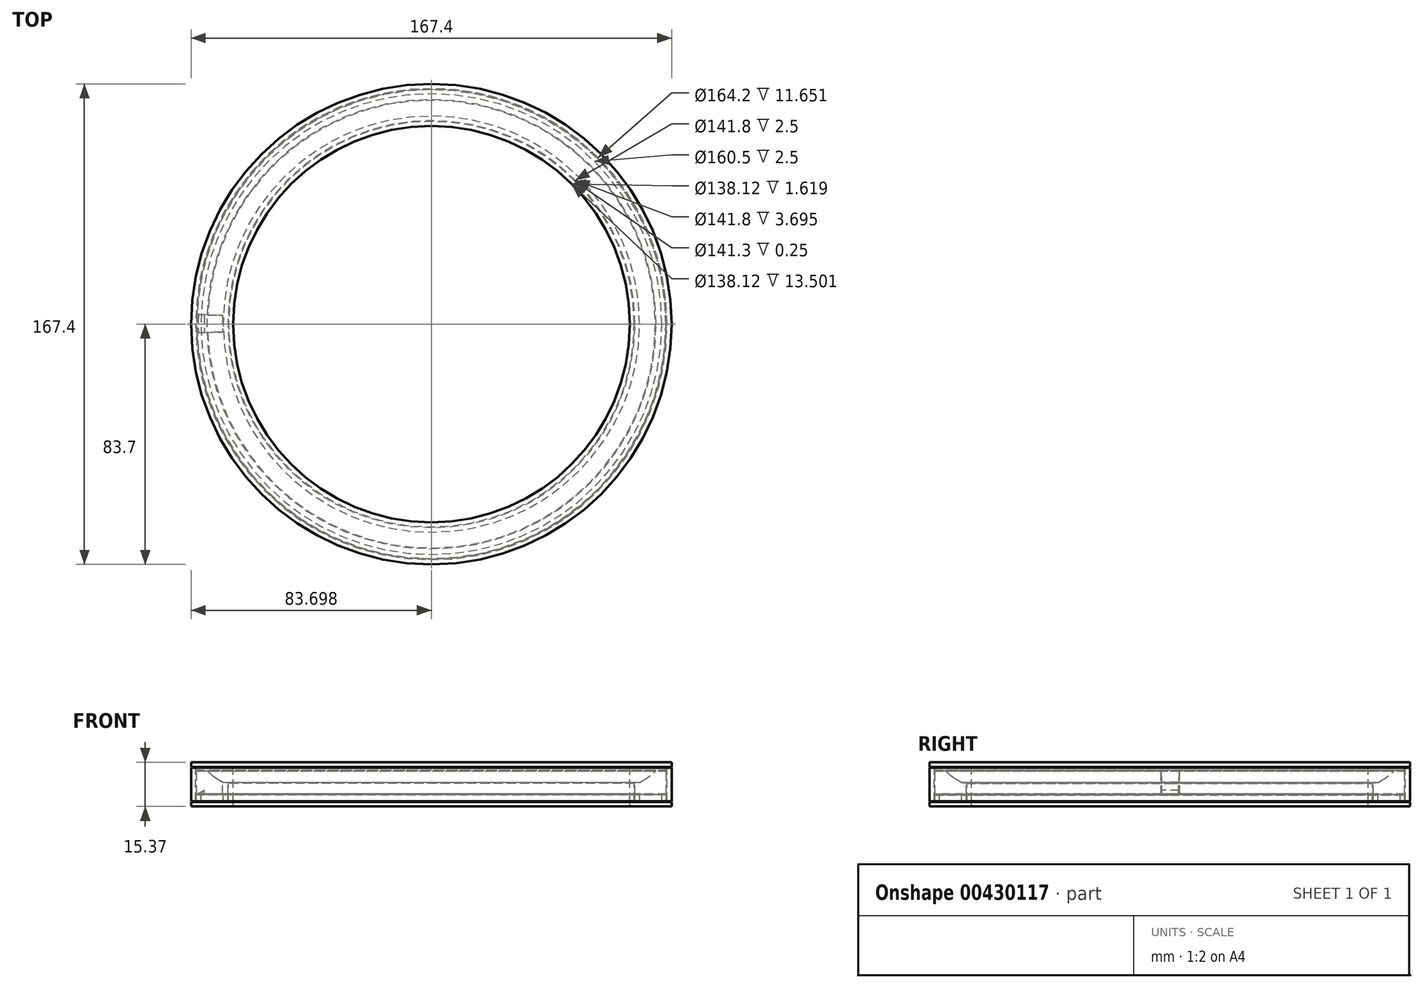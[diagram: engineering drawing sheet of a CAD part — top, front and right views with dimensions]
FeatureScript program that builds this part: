
annotation { "Feature Type Name" : "Feature", "Feature Type Description" : "" }
export const myFeature = defineFeature(function(context is Context, id is Id, definition is map)
    precondition{}
    {
        {
            var Q0;
            Q0=qCreatedBy(makeId("Front.planeOp"),FACE);
            var sketch = newSketch(context, id + "F0", { "sketchPlane" : qUnion([Q0])});
            skLineSegment(sketch, "E0", {"start": v(49.07, 29.5) * mm, "end": v(49.07, -21.25) * mm, "construction": true});
            skLineSegment(sketch, "E1", {"start": v(-23.43, 29.5) * mm, "end": v(-23.43, -21.25) * mm, "construction": true});
            skLineSegment(sketch, "E2", {"start": v(-30.18, 1.62) * mm, "end": v(-23.68, 1.62) * mm, "construction": true});
            skLineSegment(sketch, "E3", {"start": v(-23.68, 1.62) * mm, "end": v(-23.68, 4.12) * mm, "construction": true});
            skLineSegment(sketch, "E4", {"start": v(-23.68, 4.12) * mm, "end": v(-30.18, 4.12) * mm, "construction": true});
            skLineSegment(sketch, "E5", {"start": v(-30.18, 4.12) * mm, "end": v(-30.18, 1.62) * mm, "construction": true});
            skLineSegment(sketch, "E6", {"start": v(-29.18, 4.12) * mm, "end": v(-29.18, 4.92) * mm, "construction": true});
            skLineSegment(sketch, "E7", {"start": v(-29.18, 4.92) * mm, "end": v(-24.68, 4.92) * mm, "construction": true});
            skLineSegment(sketch, "E8", {"start": v(-24.68, 4.92) * mm, "end": v(-24.68, 4.12) * mm, "construction": true});
            skLineSegment(sketch, "E9", {"start": v(-35.93, 29.5) * mm, "end": v(-35.93, -21.25) * mm, "construction": true});
            skLineSegment(sketch, "E10", {"start": v(-31.18, 1.62) * mm, "end": v(-23.43, 1.62) * mm});
            skLineSegment(sketch, "E11", {"start": v(-31.18, 1.62) * mm, "end": v(-31.18, 4.12) * mm});
            skLineSegment(sketch, "E12", {"start": v(-34.74, 0.02) * mm, "end": v(-21.83, 0.02) * mm});
            skLineSegment(sketch, "E13", {"start": v(-23.43, 1.62) * mm, "end": v(-23.43, 3.24) * mm});
            skLineSegment(sketch, "E14", {"start": v(-23.43, 4.12) * mm, "end": v(-21.83, 4.12) * mm});
            skLineSegment(sketch, "E15", {"start": v(-21.83, 4.12) * mm, "end": v(-21.83, 0.02) * mm});
            skLineSegment(sketch, "E16", {"start": v(-24.68, 4.92) * mm, "end": v(-24.68, 12.8) * mm, "construction": true});
            skLineSegment(sketch, "E17", {"start": v(-29.18, 4.92) * mm, "end": v(-29.18, 12.8) * mm, "construction": true});
            skLineSegment(sketch, "E18", {"start": v(-82.01, -1.66) * mm, "end": v(-82.01, 10.37) * mm, "construction": true});
            skLineSegment(sketch, "E19", {"start": v(-23.43, 4.12) * mm, "end": v(-23.43, 1.62) * mm});
            skLineSegment(sketch, "E20", {"start": v(-72.42, 0.02) * mm, "end": v(839.7, 0.02) * mm, "construction": true});
            skLineSegment(sketch, "E21", {"start": v(-21.58, 1.87) * mm, "end": v(-21.58, 20.5) * mm});
            skLineSegment(sketch, "E22", {"start": v(-20, 1.87) * mm, "end": v(-20, 15.37) * mm});
            skLineSegment(sketch, "E23", {"start": v(-20, 15.37) * mm, "end": v(-34.63, 15.37) * mm});
            skLineSegment(sketch, "E24", {"start": v(-34.63, 13.52) * mm, "end": v(-33.03, 13.52) * mm});
            skLineSegment(sketch, "E25", {"start": v(-33.03, 13.52) * mm, "end": v(-33.03, 1.87) * mm});
            skLineSegment(sketch, "E26", {"start": v(-33.03, 1.87) * mm, "end": v(-34.63, 1.87) * mm});
            skLineSegment(sketch, "E27", {"start": v(-34.63, 1.87) * mm, "end": v(-34.63, 13.52) * mm});
            skLineSegment(sketch, "E28", {"start": v(-34.63, 0.02) * mm, "end": v(-34.74, 0.02) * mm});
            skLineSegment(sketch, "E29", {"start": v(-34.63, 0.02) * mm, "end": v(-34.63, 1.62) * mm});
            skLineSegment(sketch, "E30", {"start": v(-34.63, 1.62) * mm, "end": v(-32.78, 1.62) * mm});
            skLineSegment(sketch, "E31", {"start": v(-34.63, 15.37) * mm, "end": v(-34.63, 13.77) * mm});
            skLineSegment(sketch, "E32", {"start": v(-34.63, 13.77) * mm, "end": v(-32.78, 13.77) * mm});
            skLineSegment(sketch, "E33", {"start": v(-36.84, 4.37) * mm, "end": v(-22.3, 4.37) * mm, "construction": true});
            skLineSegment(sketch, "E34", {"start": v(-32.78, 1.62) * mm, "end": v(-32.78, 2.82) * mm});
            skLineSegment(sketch, "E35", {"start": v(-32.78, 13.77) * mm, "end": v(-32.78, 12.57) * mm});
            skLineSegment(sketch, "E36", {"start": v(-32.78, 12.57) * mm, "end": v(-28.4, 12.57) * mm});
            skLineSegment(sketch, "E37", {"start": v(-23.43, 8.31) * mm, "end": v(-21.58, 8.31) * mm});
            skLineSegment(sketch, "E38", {"start": v(-21.83, 4.37) * mm, "end": v(-31.4, 4.37) * mm});
            skLineSegment(sketch, "E39", {"start": v(-31.4, 4.37) * mm, "end": v(-32.78, 4.37) * mm});
            skLineSegment(sketch, "E40.0", {"start": v(-32.78, 12.32) * mm, "end": v(-28.4, 12.32) * mm});
            skLineSegment(sketch, "E41", {"start": v(-32.78, 12.32) * mm, "end": v(-32.78, 4.37) * mm});
            skLineSegment(sketch, "E42", {"start": v(-23.43, 8.31) * mm, "end": v(-24.68, 9.04) * mm});
            skLineSegment(sketch, "E43", {"start": v(-22.53, 10.28) * mm, "end": v(-40.3, 0.02) * mm, "construction": true});
            skArc(sketch, "E44", {"start": v(-24.68, 9.04) * mm, "mid": v(-27.06, 10.64) * mm, "end": v(-29.18, 12.57) * mm});
            skLineSegment(sketch, "E45", {"start": v(-29.18, 12.57) * mm, "end": v(-28.4, 12.57) * mm});
            skArc(sketch, "E46.0", {"start": v(-24.78, 8.8) * mm, "mid": v(-27.19, 10.43) * mm, "end": v(-29.34, 12.37) * mm});
            skLineSegment(sketch, "E47", {"start": v(-29.29, 12.32) * mm, "end": v(-28.4, 12.32) * mm});
            skLineSegment(sketch, "E48.0", {"start": v(-23.5, 8.06) * mm, "end": v(-24.8, 8.81) * mm});
            skLineSegment(sketch, "E49.0", {"start": v(-23.5, 8.06) * mm, "end": v(-21.56, 8.06) * mm});
            skLineSegment(sketch, "E50", {"start": v(-21.83, 4.37) * mm, "end": v(-21.83, 8.06) * mm});
            skLineSegment(sketch, "E51", {"start": v(-23.43, 4.37) * mm, "end": v(-23.43, 8.06) * mm});
            skLineSegment(sketch, "E52", {"start": v(-32.78, 4) * mm, "end": v(-32.58, 4.12) * mm});
            skLineSegment(sketch, "E53", {"start": v(-32.78, 2.82) * mm, "end": v(-32.78, 4) * mm});
            skLineSegment(sketch, "E54", {"start": v(-31.18, 4.12) * mm, "end": v(-32.58, 4.12) * mm});
            skLineSegment(sketch, "E55", {"start": v(-32.78, 4) * mm, "end": v(-30.18, 5.5) * mm, "construction": true});
            skLineSegment(sketch, "E56", {"start": v(-30.05, 5.58) * mm, "end": v(-32.14, 4.37) * mm});
            skLineSegment(sketch, "E57", {"start": v(-30.05, 5.58) * mm, "end": v(-30.05, 4.37) * mm});
            skLineSegment(sketch, "E58", {"start": v(-30.05, 4.37) * mm, "end": v(-32.14, 4.37) * mm});
            skLineSegment(sketch, "E59", {"start": v(-21.58, 1.87) * mm, "end": v(-20, 1.87) * mm});
            skLineSegment(sketch, "E60", {"start": v(-21.83, 1.62) * mm, "end": v(-20, 1.62) * mm});
            skLineSegment(sketch, "E61", {"start": v(-20, 1.62) * mm, "end": v(-20, 0) * mm});
            skLineSegment(sketch, "E62", {"start": v(-20, 0) * mm, "end": v(-21.83, 0.02) * mm});
            skSolve(sketch);
        }
        {
            var Q0;
            Q0=makeQuery(id+"F0.imprint","IMPRINT",FACE,{"disambiguationData":[TD([[makeQuery(id+"F0.imprint","IMPRINT",EDGE,{"derivedFrom":sQuery(id+"F0.wireOp",EDGE,"E40.0")}),-1.0]])]});
            var Q1;
            {var subQ0=sQuery(id+"F0.wireOp",EDGE,"E50");Q1=makeQuery(id+"F0.imprint","IMPRINT",FACE,{"disambiguationData":[TD([[makeQuery(id+"F0.imprint","IMPRINT",EDGE,{"derivedFrom":subQ0}),1.0]])]});}
            var Q2;
            {var subQ3=sQuery(id+"F0.wireOp",EDGE,"nZakiuLn-CLJS-k8i2-04lO-UVL3UxqrP7IB");Q2=makeQuery(id+"F0.imprint","IMPRINT",FACE,{"disambiguationData":[TD([[makeQuery(id+"F0.imprint","IMPRINT",EDGE,{"derivedFrom":subQ3}),1.0]])]});}
            var Q3;
            {var subQ0=sQuery(id+"F0.wireOp",EDGE,"E56");Q3=makeQuery(id+"F0.imprint","IMPRINT",FACE,{"disambiguationData":[TD([[makeQuery(id+"F0.imprint","IMPRINT",EDGE,{"derivedFrom":subQ0}),1.0]])]});}
            var Q4;
            Q4=sQuery(id+"F0.wireOp",EDGE,"E0");
            revolve(context, id + "F1", {"entities" : qUnion([Q0, Q1, Q2, Q3]), "axis" : qUnion([Q4]), "revolveType" : RevolveType.FULL});
        }
        {
            var Q0;
            Q0=makeQuery(id+"F1.opRevolve","SWEPT_FACE",FACE,{"disambiguationData":[OSD([sQuery(id+"F0.wireOp",EDGE,"E40.0"),sQuery(id+"F0.wireOp",EDGE,"E47")])]});
            var sketch = newSketch(context, id + "F2", { "sketchPlane" : qUnion([Q0])});
            skPoint(sketch, "E63.0", {"position": v(-30.18, 0) * mm});
            skPoint(sketch, "E64.0", {"position": v(-23.68, 0) * mm});
            skLineSegment(sketch, "E65.bottom", {"start": v(-23.68, -2.74) * mm, "end": v(-36.08, -3.2) * mm});
            skLineSegment(sketch, "E66", {"start": v(-36.07, 3.54) * mm, "end": v(49.07, 0) * mm, "construction": true});
            skLineSegment(sketch, "E67", {"start": v(49.07, 0) * mm, "end": v(-36.08, -3.2) * mm, "construction": true});
            skLineSegment(sketch, "E68", {"start": v(-34.44, 3.47) * mm, "end": v(-20.06, 2.87) * mm});
            skLineSegment(sketch, "E69", {"start": v(-20.06, -2.6) * mm, "end": v(-34.44, -3.14) * mm});
            skLineSegment(sketch, "E70", {"start": v(-34.44, -3.14) * mm, "end": v(-34.44, 3.47) * mm});
            skArc(sketch, "E71", {"start": v(-23.68, 0) * mm, "mid": v(-23.67, 1.5) * mm, "end": v(-23.62, 3.02) * mm});
            skArc(sketch, "E72", {"start": v(-23.68, 0) * mm, "mid": v(-23.67, -1.37) * mm, "end": v(-23.63, -2.74) * mm});
            skSolve(sketch);
        }
        {
            var Q0;
            Q0=qSketchRegion(id+"F2",true);
            var Q1;
            Q1=makeQuery(id+"F1.opRevolve","SWEPT_FACE",FACE,{"disambiguationData":[OSD([sQuery(id+"F0.wireOp",EDGE,"E38"),sQuery(id+"F0.wireOp",EDGE,"E39"),sQuery(id+"F0.wireOp",EDGE,"E58")])]});
            extrude(context, id + "F3", {"entities" : qUnion([Q0]), "operationType" : NewBodyOperationType.REMOVE, "endBound" : BoundingType.UP_TO_SURFACE, "oppositeDirection" : true, "endBoundEntityFace" : qUnion([Q1]), "depth" : 25 * mm});
        }
        {
            var Q0;
            {var subQ0=sQuery(id+"F0.wireOp",EDGE,"E56");Q0=makeQuery(id+"F0.imprint","IMPRINT",FACE,{"disambiguationData":[TD([[makeQuery(id+"F0.imprint","IMPRINT",EDGE,{"derivedFrom":subQ0}),1.0]])]});}
            var Q1;
            Q1=sQuery(id+"F0.wireOp",EDGE,"E0");
            revolve(context, id + "F4", {"operationType" : NewBodyOperationType.ADD, "entities" : qUnion([Q0]), "axis" : qUnion([Q1]), "revolveType" : RevolveType.FULL});
        }
        {
            var Q0;
            {var subQ2=sQuery(id+"F0.wireOp",EDGE,"E60");Q0=makeQuery(id+"F0.imprint","IMPRINT",FACE,{"disambiguationData":[TD([[makeQuery(id+"F0.imprint","IMPRINT",EDGE,{"derivedFrom":subQ2}),-1.0]])]});}
            var Q1;
            {var subQ2=sQuery(id+"F0.wireOp",EDGE,"E10");Q1=makeQuery(id+"F0.imprint","IMPRINT",FACE,{"disambiguationData":[TD([[makeQuery(id+"F0.imprint","IMPRINT",EDGE,{"derivedFrom":subQ2}),-1.0]])]});}
            var Q2;
            Q2=sQuery(id+"F0.wireOp",EDGE,"E0");
            revolve(context, id + "F5", {"entities" : qUnion([Q0, Q1]), "axis" : qUnion([Q2]), "revolveType" : RevolveType.FULL});
        }
        {
            var Q0;
            {var subQ4=sQuery(id+"F0.wireOp",EDGE,"E31");Q0=makeQuery(id+"F0.imprint","IMPRINT",FACE,{"disambiguationData":[TD([[makeQuery(id+"F0.imprint","IMPRINT",EDGE,{"derivedFrom":subQ4}),1.0]])]});}
            var Q1;
            {var subQ0=sQuery(id+"F0.wireOp",EDGE,"u2Rdq3c2-eWa1-kzH8-av5P-0K82xw47kb6N");Q1=makeQuery(id+"F0.imprint","IMPRINT",FACE,{"disambiguationData":[TD([[makeQuery(id+"F0.imprint","IMPRINT",EDGE,{"derivedFrom":subQ0}),1.0]])]});}
            var Q2;
            {var subQ0=sQuery(id+"F0.wireOp",EDGE,"E22");Q2=makeQuery(id+"F0.imprint","IMPRINT",FACE,{"disambiguationData":[TD([[makeQuery(id+"F0.imprint","IMPRINT",EDGE,{"derivedFrom":subQ0}),1.0]])]});}
            var Q3;
            Q3=sQuery(id+"F0.wireOp",EDGE,"E0");
            revolve(context, id + "F6", {"entities" : qUnion([Q0, Q1, Q2]), "axis" : qUnion([Q3]), "revolveType" : RevolveType.FULL});
        }
        {
            var Q0;
            Q0=makeQuery(id+"F0.imprint","IMPRINT",FACE,{"disambiguationData":[TD([[makeQuery(id+"F0.imprint","IMPRINT",EDGE,{"derivedFrom":sQuery(id+"F0.wireOp",EDGE,"E24")}),-1.0]])]});
            var Q1;
            Q1=sQuery(id+"F0.wireOp",EDGE,"E0");
            revolve(context, id + "F7", {"entities" : qUnion([Q0]), "axis" : qUnion([Q1]), "revolveType" : RevolveType.FULL});
        }
    });
